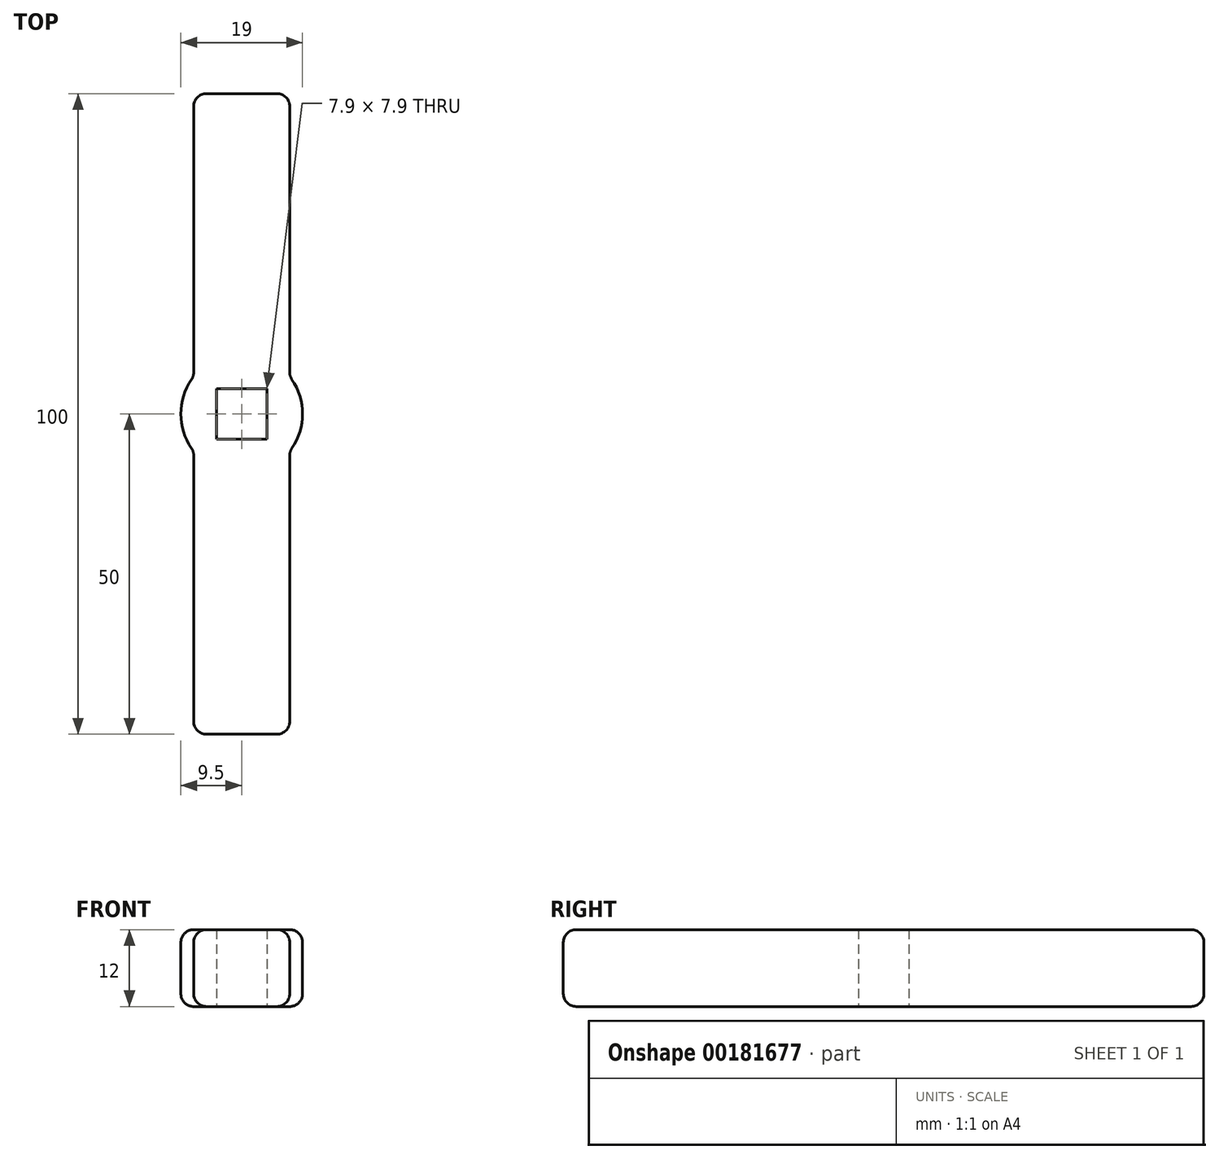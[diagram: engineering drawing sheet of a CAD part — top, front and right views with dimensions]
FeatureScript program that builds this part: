
annotation { "Feature Type Name" : "Feature", "Feature Type Description" : "" }
export const myFeature = defineFeature(function(context is Context, id is Id, definition is map)
    precondition{}
    {
        {
            var Q0;
            Q0=qCreatedBy(makeId("Top.planeOp"),FACE);
            var sketch = newSketch(context, id + "F0", { "sketchPlane" : qUnion([Q0])});
            skLineSegment(sketch, "E0.bottom", {"start": v(-7.5, -50) * mm, "end": v(7.5, -50) * mm});
            skLineSegment(sketch, "E0.top", {"start": v(-7.5, 50) * mm, "end": v(7.5, 50) * mm});
            skLineSegment(sketch, "E0.left", {"start": v(-7.5, -50) * mm, "end": v(-7.5, -5.83) * mm});
            skLineSegment(sketch, "E0.right", {"start": v(7.5, -50) * mm, "end": v(7.5, -5.83) * mm});
            skPoint(sketch, "E0.middle", {"position": v(0, 0) * mm});
            skLineSegment(sketch, "E1.bottom", {"start": v(3.95, -3.95) * mm, "end": v(-3.95, -3.95) * mm});
            skLineSegment(sketch, "E1.top", {"start": v(3.95, 3.95) * mm, "end": v(-3.95, 3.95) * mm});
            skLineSegment(sketch, "E1.left", {"start": v(3.95, -3.95) * mm, "end": v(3.95, 3.95) * mm});
            skLineSegment(sketch, "E1.right", {"start": v(-3.95, -3.95) * mm, "end": v(-3.95, 3.95) * mm});
            skArc(sketch, "E2", {"start": v(-7.5, 5.83) * mm, "mid": v(-9.5, 0) * mm, "end": v(-7.5, -5.83) * mm});
            skLineSegment(sketch, "E3.trimOffspring", {"start": v(-7.5, 5.83) * mm, "end": v(-7.5, 50) * mm});
            skLineSegment(sketch, "E4.trimOffspring", {"start": v(7.5, 5.83) * mm, "end": v(7.5, 50) * mm});
            skArc(sketch, "E5.trimOffspring", {"start": v(7.5, -5.83) * mm, "mid": v(9.5, 0) * mm, "end": v(7.5, 5.83) * mm});
            skSolve(sketch);
        }
        {
            var Q0;
            Q0 = qSketchRegion(id + "F0", true);
            extrude(context, id + "F1", {"entities" : qUnion([Q0]), "depth" : 12 * mm});
        }
        {
            var Q0;
            Q0=makeQuery(id+"F1.opExtrude","CAP_EDGE",EDGE,{"disambiguationData":[OSD([sQuery(id+"F0.wireOp",EDGE,"E0.bottom")])],"isStart":false});
            var Q1;
            Q1=makeQuery(id+"F1.opExtrude","CAP_EDGE",EDGE,{"disambiguationData":[OSD([sQuery(id+"F0.wireOp",EDGE,"E0.right")])],"isStart":false});
            var Q2;
            Q2=makeQuery(id+"F1.opExtrude","CAP_EDGE",EDGE,{"disambiguationData":[OSD([sQuery(id+"F0.wireOp",EDGE,"E0.left")])],"isStart":false});
            var Q3;
            Q3=makeQuery(id+"F1.opExtrude","CAP_EDGE",EDGE,{"disambiguationData":[OSD([sQuery(id+"F0.wireOp",EDGE,"E4.trimOffspring")])],"isStart":false});
            var Q4;
            Q4=makeQuery(id+"F1.opExtrude","CAP_EDGE",EDGE,{"disambiguationData":[OSD([sQuery(id+"F0.wireOp",EDGE,"E3.trimOffspring")])],"isStart":false});
            var Q5;
            Q5=makeQuery(id+"F1.opExtrude","CAP_EDGE",EDGE,{"disambiguationData":[OSD([sQuery(id+"F0.wireOp",EDGE,"E5.trimOffspring")])],"isStart":false});
            var Q6;
            Q6=makeQuery(id+"F1.opExtrude","CAP_EDGE",EDGE,{"disambiguationData":[OSD([sQuery(id+"F0.wireOp",EDGE,"E2")])],"isStart":false});
            var Q7;
            Q7=makeQuery(id+"F1.opExtrude","CAP_EDGE",EDGE,{"disambiguationData":[OSD([sQuery(id+"F0.wireOp",EDGE,"E0.top")])],"isStart":false});
            var Q8;
            Q8=makeQuery(id+"F1.opExtrude","SWEPT_EDGE",EDGE,{"disambiguationData":[OSD([sQuery(id+"F0.wireOp",EDGE,"E0.bottom"),sQuery(id+"F0.wireOp",EDGE,"E0.right")])]});
            var Q9;
            Q9=makeQuery(id+"F1.opExtrude","CAP_EDGE",EDGE,{"disambiguationData":[OSD([sQuery(id+"F0.wireOp",EDGE,"E0.right")])],"isStart":true});
            var Q10;
            Q10=makeQuery(id+"F1.opExtrude","CAP_EDGE",EDGE,{"disambiguationData":[OSD([sQuery(id+"F0.wireOp",EDGE,"E0.bottom")])],"isStart":true});
            var Q11;
            Q11=makeQuery(id+"F1.opExtrude","SWEPT_EDGE",EDGE,{"disambiguationData":[OSD([sQuery(id+"F0.wireOp",EDGE,"E0.bottom"),sQuery(id+"F0.wireOp",EDGE,"E0.left")])]});
            var Q12;
            Q12=makeQuery(id+"F1.opExtrude","CAP_EDGE",EDGE,{"disambiguationData":[OSD([sQuery(id+"F0.wireOp",EDGE,"E2")])],"isStart":true});
            var Q13;
            Q13=makeQuery(id+"F1.opExtrude","CAP_EDGE",EDGE,{"disambiguationData":[OSD([sQuery(id+"F0.wireOp",EDGE,"E0.left")])],"isStart":true});
            var Q14;
            Q14=makeQuery(id+"F1.opExtrude","CAP_EDGE",EDGE,{"disambiguationData":[OSD([sQuery(id+"F0.wireOp",EDGE,"E3.trimOffspring")])],"isStart":true});
            var Q15;
            Q15=makeQuery(id+"F1.opExtrude","CAP_EDGE",EDGE,{"disambiguationData":[OSD([sQuery(id+"F0.wireOp",EDGE,"E4.trimOffspring")])],"isStart":true});
            var Q16;
            Q16=makeQuery(id+"F1.opExtrude","CAP_EDGE",EDGE,{"disambiguationData":[OSD([sQuery(id+"F0.wireOp",EDGE,"E5.trimOffspring")])],"isStart":true});
            var Q17;
            Q17=makeQuery(id+"F1.opExtrude","SWEPT_EDGE",EDGE,{"disambiguationData":[OSD([sQuery(id+"F0.wireOp",EDGE,"E0.top"),sQuery(id+"F0.wireOp",EDGE,"E4.trimOffspring")])]});
            var Q18;
            Q18=makeQuery(id+"F1.opExtrude","SWEPT_EDGE",EDGE,{"disambiguationData":[OSD([sQuery(id+"F0.wireOp",EDGE,"E0.top"),sQuery(id+"F0.wireOp",EDGE,"E3.trimOffspring")])]});
            var Q19;
            Q19=makeQuery(id+"F1.opExtrude","CAP_EDGE",EDGE,{"disambiguationData":[OSD([sQuery(id+"F0.wireOp",EDGE,"E0.top")])],"isStart":true});
            var Q20;
            Q20=makeQuery(id+"F1.opExtrude","SWEPT_EDGE",EDGE,{"disambiguationData":[OSD([sQuery(id+"F0.wireOp",EDGE,"E4.trimOffspring"),sQuery(id+"F0.wireOp",EDGE,"E5.trimOffspring")])]});
            var Q21;
            Q21=makeQuery(id+"F1.opExtrude","SWEPT_EDGE",EDGE,{"disambiguationData":[OSD([sQuery(id+"F0.wireOp",EDGE,"E0.right"),sQuery(id+"F0.wireOp",EDGE,"E5.trimOffspring")])]});
            var Q22;
            Q22=makeQuery(id+"F1.opExtrude","SWEPT_EDGE",EDGE,{"disambiguationData":[OSD([sQuery(id+"F0.wireOp",EDGE,"E0.left"),sQuery(id+"F0.wireOp",EDGE,"E2")])]});
            var Q23;
            Q23=makeQuery(id+"F1.opExtrude","SWEPT_EDGE",EDGE,{"disambiguationData":[OSD([sQuery(id+"F0.wireOp",EDGE,"E2"),sQuery(id+"F0.wireOp",EDGE,"E3.trimOffspring")])]});
            fillet(context, id + "F2", {"entities" : qUnion([Q0, Q1, Q2, Q3, Q4, Q5, Q6, Q7, Q8, Q9, Q10, Q11, Q12, Q13, Q14, Q15, Q16, Q17, Q18, Q19, Q20, Q21, Q22, Q23]), "radius" : 2 * mm, "tangentPropagation" : true, "allowEdgeOverflow" : false});
        }
    });
